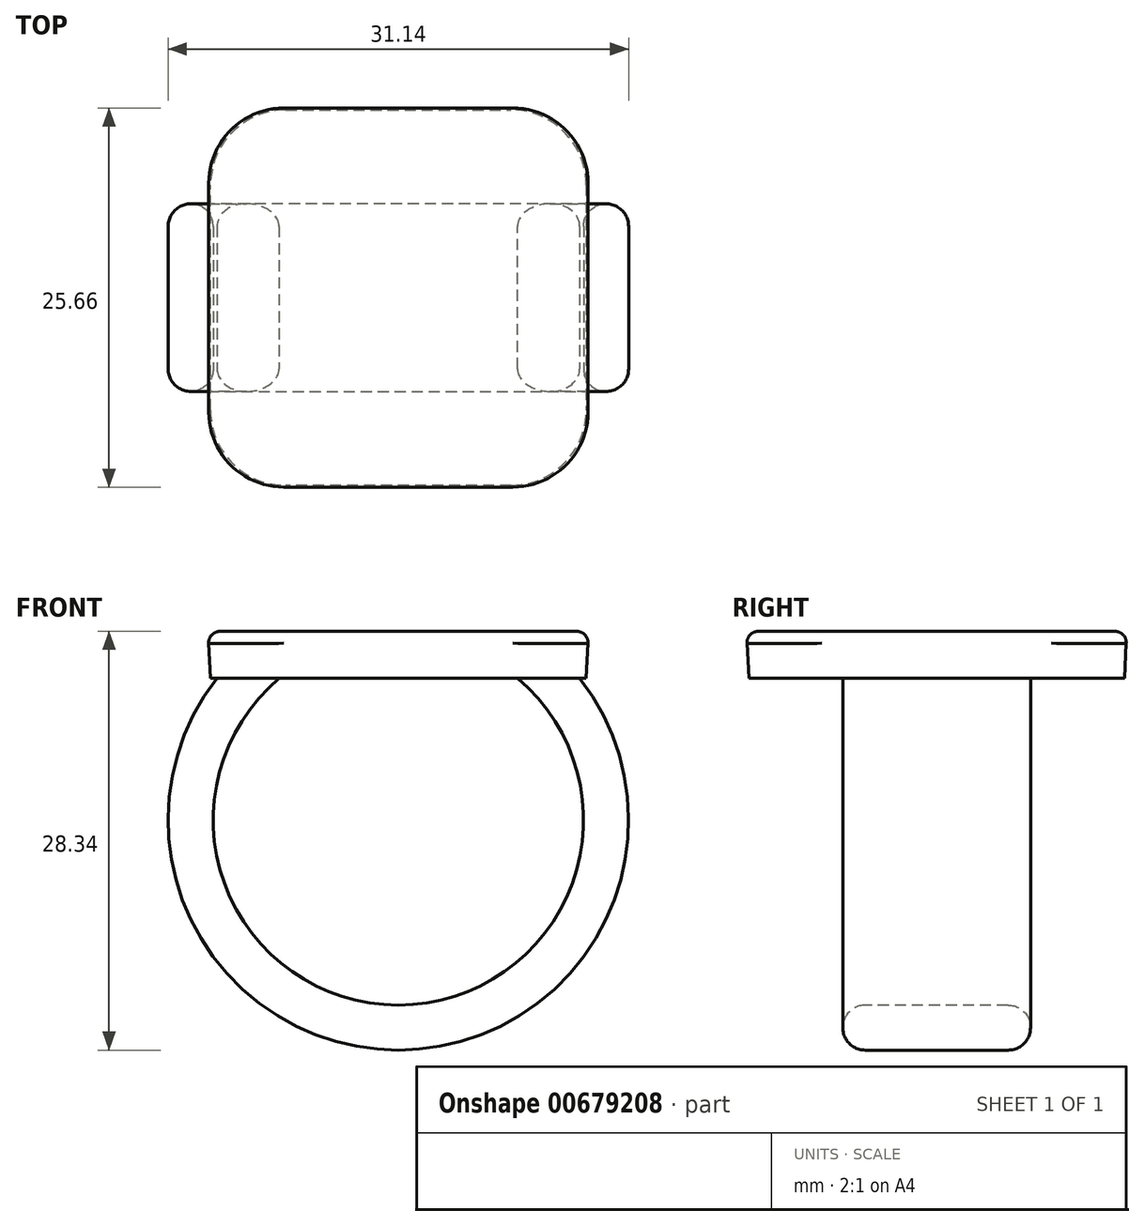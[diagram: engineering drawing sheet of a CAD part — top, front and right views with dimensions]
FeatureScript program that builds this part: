
annotation { "Feature Type Name" : "Feature", "Feature Type Description" : "" }
export const myFeature = defineFeature(function(context is Context, id is Id, definition is map)
    precondition{}
    {
        {
            var Q0;
            Q0=qCreatedBy(makeId("Top.planeOp"),FACE);
            var sketch = newSketch(context, id + "F0", { "sketchPlane" : qUnion([Q0])});
            skLineSegment(sketch, "E0.bottom", {"start": v(-12.7, -12.7) * mm, "end": v(12.7, -12.7) * mm});
            skLineSegment(sketch, "E0.top", {"start": v(-12.7, 12.7) * mm, "end": v(12.7, 12.7) * mm});
            skLineSegment(sketch, "E0.left", {"start": v(-12.7, -12.7) * mm, "end": v(-12.7, 12.7) * mm});
            skLineSegment(sketch, "E0.right", {"start": v(12.7, -12.7) * mm, "end": v(12.7, 12.7) * mm});
            skPoint(sketch, "E0.middle", {"position": v(0, 0) * mm});
            skSolve(sketch);
        }
        {
            var Q0;
            Q0=makeQuery(id+"F0.imprint","IMPRINT",FACE,{"disambiguationData":[TD([[makeQuery(id+"F0.imprint","IMPRINT",EDGE,{"derivedFrom":sQuery(id+"F0.wireOp",EDGE,"E0.bottom")}),1.0]])]});
            extrude(context, id + "F1", {"entities" : qUnion([Q0]), "depth" : 3.17 * mm, "offsetDistance" : 25.4 * mm, "hasDraft" : true, "draftAngle" : 3 * degree});
        }
        {
            var Q0;
            Q0=qCreatedBy(makeId("Front.planeOp"),FACE);
            var sketch = newSketch(context, id + "F2", { "sketchPlane" : qUnion([Q0])});
            skArc(sketch, "E1", {"start": v(-10.16, 0) * mm, "mid": v(0, -23.56) * mm, "end": v(10.16, 0) * mm});
            skSolve(sketch);
        }
        {
            var Q0;
            Q0=makeQuery(id+"F1.opExtrude","CAP_FACE",FACE,{"disambiguationData":[OSD([sQuery(id+"F0.wireOp",EDGE,"E0.bottom"),sQuery(id+"F0.wireOp",EDGE,"E0.top"),sQuery(id+"F0.wireOp",EDGE,"E0.left"),sQuery(id+"F0.wireOp",EDGE,"E0.right")])],"isStart":true});
            var sketch = newSketch(context, id + "F3", { "sketchPlane" : qUnion([Q0])});
            skLineSegment(sketch, "E2.bottom", {"start": v(-8.05, -6.35) * mm, "end": v(-12.27, -6.35) * mm});
            skLineSegment(sketch, "E2.top", {"start": v(-8.05, 6.35) * mm, "end": v(-12.27, 6.35) * mm});
            skLineSegment(sketch, "E2.left", {"start": v(-8.05, -6.35) * mm, "end": v(-8.05, 6.35) * mm});
            skLineSegment(sketch, "E2.right", {"start": v(-12.27, -6.35) * mm, "end": v(-12.27, 6.35) * mm});
            skPoint(sketch, "E2.middle", {"position": v(-10.16, 0) * mm});
            skSolve(sketch);
        }
        {
            var Q0;
            Q0 = qSketchRegion(id + "F3", true);
            var Q1;
            Q1 = qConstructionFilter(qBodyType(qCreatedBy(id + "F2" ,EDGE), BodyType.WIRE), ConstructionObject.NO);
            sweep(context, id + "F4", {"operationType" : NewBodyOperationType.ADD, "profiles" : qUnion([Q0]), "path" : qUnion([Q1])});
        }
        {
            var Q0;
            Q0=qCreatedBy(makeId("Front.planeOp"),FACE);
            var sketch = newSketch(context, id + "F5", { "sketchPlane" : qUnion([Q0])});
            skLineSegment(sketch, "E3.0", {"start": v(-12.7, 0) * mm, "end": v(-8.05, 0) * mm});
            skLineSegment(sketch, "E3.1", {"start": v(10.04, -2.1) * mm, "end": v(10.16, 0) * mm});
            skArc(sketch, "E3.2", {"start": v(10.04, -2.1) * mm, "mid": v(9.1, -1) * mm, "end": v(8.05, 0) * mm});
            skPoint(sketch, "E4.orphan", {"position": v(-8.05, 0) * mm});
            skLineSegment(sketch, "E5.trimOffspring", {"start": v(8.05, 0) * mm, "end": v(12.7, 0) * mm});
            skSolve(sketch);
        }
        {
            var Q0;
            Q0 = qSketchRegion(id + "F5", true);
            var Q1;
            Q1=makeQuery(id+"F4.opSweep","SWEPT_FACE",FACE,{"disambiguationData":[OSD([sQuery(id+"F2.wireOp",EDGE,"E1"),sQuery(id+"F3.wireOp",EDGE,"E2.top")])]});
            var Q2;
            Q2=makeQuery(id+"F4.opSweep","SWEPT_FACE",FACE,{"disambiguationData":[OSD([sQuery(id+"F2.wireOp",EDGE,"E1"),sQuery(id+"F3.wireOp",EDGE,"E2.bottom")])]});
            extrude(context, id + "F6", {"entities" : qUnion([Q0]), "operationType" : NewBodyOperationType.ADD, "endBound" : BoundingType.UP_TO_SURFACE, "depth" : 25.4 * mm, "endBoundEntityFace" : qUnion([Q1]), "offsetDistance" : 25.4 * mm, "hasSecondDirection" : true, "secondDirectionBound" : SecondDirectionBoundingType.UP_TO_SURFACE, "secondDirectionOppositeDirection" : true, "secondDirectionDepth" : 25.4 * mm, "secondDirectionBoundEntityFace" : qUnion([Q2])});
        }
        {
            var Q0;
            Q0=makeQuery(id+"F1.opExtrude","SWEPT_EDGE",EDGE,{"disambiguationData":[OSD([sQuery(id+"F0.wireOp",EDGE,"E0.bottom"),sQuery(id+"F0.wireOp",EDGE,"E0.right")])]});
            var Q1;
            Q1=makeQuery(id+"F1.opExtrude","SWEPT_EDGE",EDGE,{"disambiguationData":[OSD([sQuery(id+"F0.wireOp",EDGE,"E0.bottom"),sQuery(id+"F0.wireOp",EDGE,"E0.left")])]});
            var Q2;
            Q2=makeQuery(id+"F1.opExtrude","SWEPT_EDGE",EDGE,{"disambiguationData":[OSD([sQuery(id+"F0.wireOp",EDGE,"E0.top"),sQuery(id+"F0.wireOp",EDGE,"E0.right")])]});
            var Q3;
            Q3=makeQuery(id+"F1.opExtrude","SWEPT_EDGE",EDGE,{"disambiguationData":[OSD([sQuery(id+"F0.wireOp",EDGE,"E0.top"),sQuery(id+"F0.wireOp",EDGE,"E0.left")])]});
            fillet(context, id + "F7", {"entities" : qUnion([Q0, Q1, Q2, Q3]), "radius" : 5.08 * mm, "tangentPropagation" : true, "allowEdgeOverflow" : false});
        }
        {
            var Q0;
            Q0=makeQuery(id+"F4.opSweep","SWEPT_EDGE",EDGE,{"disambiguationData":[OSD([sQuery(id+"F2.wireOp",EDGE,"E1"),sQuery(id+"F3.wireOp",EDGE,"E2.bottom"),sQuery(id+"F3.wireOp",EDGE,"E2.right")])]});
            var Q1;
            {var subQ0=sQuery(id+"F3.wireOp",EDGE,"E2.bottom");var subQ1=sQuery(id+"F2.wireOp",EDGE,"E1");Q1=makeQuery(id+"F6.boolean.opBoolean","MERGE",EDGE,{"derivedFrom":[makeQuery(id+"F4.opSweep","SWEPT_EDGE",EDGE,{"disambiguationData":[OSD([subQ1,subQ0,sQuery(id+"F3.wireOp",EDGE,"E2.left")])]}),makeQuery(id+"F6.opExtrude","TWEAK_EDGE",EDGE,{"derivedFrom":[makeQuery(id+"F4.opSweep","SWEPT_FACE",FACE,{"disambiguationData":[OSD([subQ1,subQ0])]}),makeQuery(id+"F5.imprint","IMPRINT",EDGE,{"derivedFrom":sQuery(id+"F5.wireOp",EDGE,"E3.2")})]})]});}
            var Q2;
            Q2=makeQuery(id+"F4.opSweep","SWEPT_EDGE",EDGE,{"disambiguationData":[OSD([sQuery(id+"F2.wireOp",EDGE,"E1"),sQuery(id+"F3.wireOp",EDGE,"E2.top"),sQuery(id+"F3.wireOp",EDGE,"E2.right")])]});
            var Q3;
            {var subQ0=sQuery(id+"F3.wireOp",EDGE,"E2.top");var subQ1=sQuery(id+"F2.wireOp",EDGE,"E1");Q3=makeQuery(id+"F6.boolean.opBoolean","MERGE",EDGE,{"derivedFrom":[makeQuery(id+"F4.opSweep","SWEPT_EDGE",EDGE,{"disambiguationData":[OSD([subQ1,subQ0,sQuery(id+"F3.wireOp",EDGE,"E2.left")])]}),makeQuery(id+"F6.opExtrude","TWEAK_EDGE",EDGE,{"derivedFrom":[makeQuery(id+"F4.opSweep","SWEPT_FACE",FACE,{"disambiguationData":[OSD([subQ1,subQ0])]}),makeQuery(id+"F5.imprint","IMPRINT",EDGE,{"derivedFrom":sQuery(id+"F5.wireOp",EDGE,"E3.2")})]})]});}
            fillet(context, id + "F8", {"entities" : qUnion([Q0, Q1, Q2, Q3]), "radius" : 1.52 * mm, "tangentPropagation" : true, "allowEdgeOverflow" : false});
        }
        {
            var Q0;
            Q0=makeQuery(id+"F1.opExtrude","CAP_FACE",FACE,{"disambiguationData":[OSD([sQuery(id+"F0.wireOp",EDGE,"E0.bottom"),sQuery(id+"F0.wireOp",EDGE,"E0.top"),sQuery(id+"F0.wireOp",EDGE,"E0.left"),sQuery(id+"F0.wireOp",EDGE,"E0.right")])],"isStart":false});
            fillet(context, id + "F9", {"entities" : qUnion([Q0]), "radius" : 0.76 * mm, "tangentPropagation" : true, "allowEdgeOverflow" : false});
        }
    });
